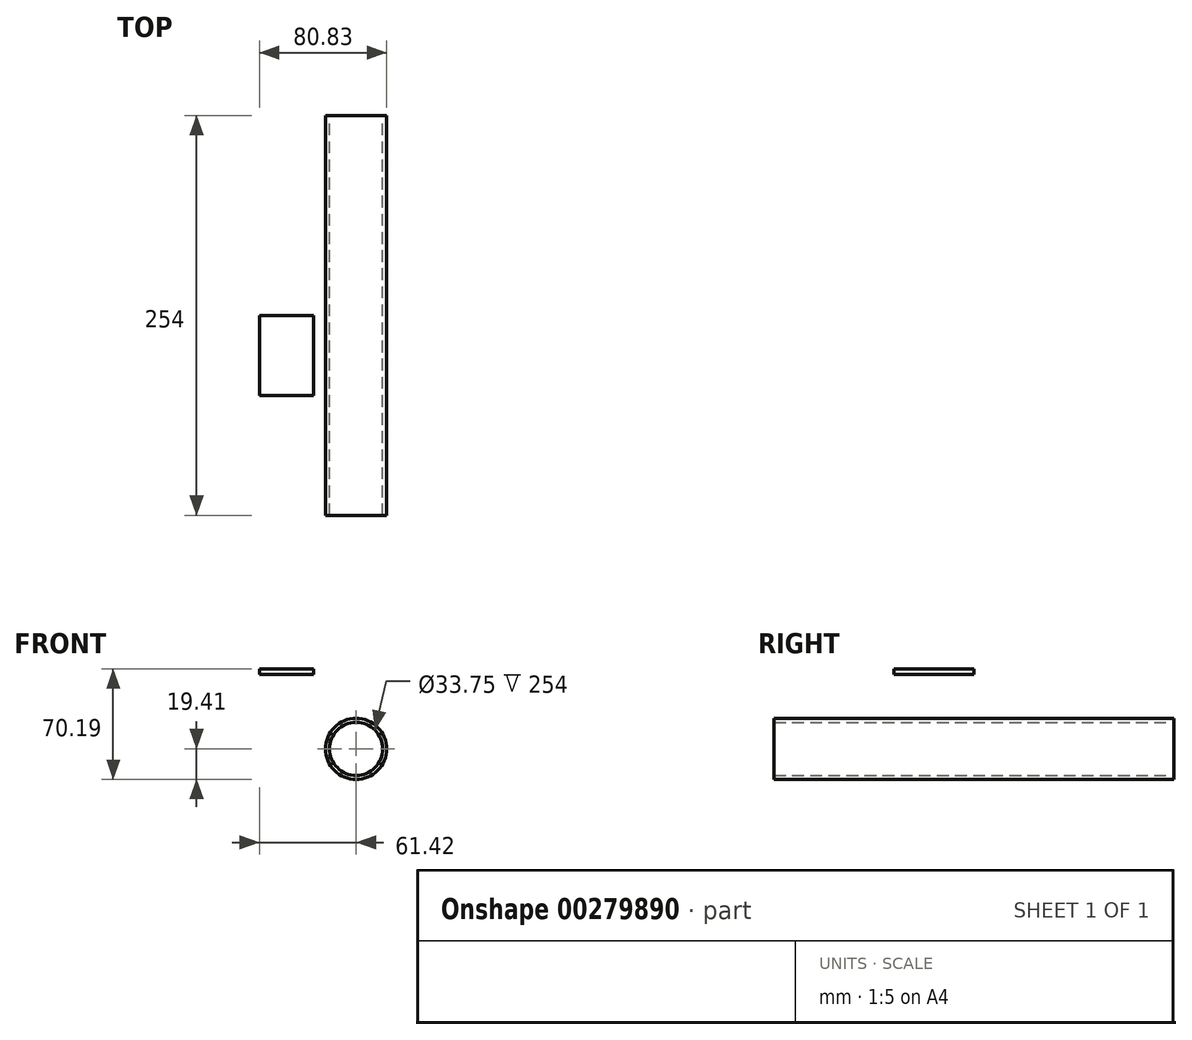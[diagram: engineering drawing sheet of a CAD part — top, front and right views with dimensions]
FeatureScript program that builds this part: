
annotation { "Feature Type Name" : "Feature", "Feature Type Description" : "" }
export const myFeature = defineFeature(function(context is Context, id is Id, definition is map)
    precondition{}
    {
        {
            var Q0;
            Q0=qCreatedBy(makeId("Front.planeOp"),FACE);
            var sketch = newSketch(context, id + "F0", { "sketchPlane" : qUnion([Q0])});
            skCircle(sketch, "E0", {"center": v(0, 0) * mm, "radius": 19.4 * mm});
            skCircle(sketch, "E1", {"center": v(0, 0) * mm, "radius": 16.88 * mm});
            skLineSegment(sketch, "E2.bottom", {"start": v(-61.42, 50.78) * mm, "end": v(-27, 50.78) * mm});
            skLineSegment(sketch, "E2.top", {"start": v(-61.42, 47.27) * mm, "end": v(-27, 47.27) * mm});
            skLineSegment(sketch, "E2.left", {"start": v(-61.42, 50.78) * mm, "end": v(-61.42, 47.27) * mm});
            skLineSegment(sketch, "E2.right", {"start": v(-27, 50.78) * mm, "end": v(-27, 47.27) * mm});
            skPoint(sketch, "E3", {"position": v(0, 19.4) * mm});
            skPoint(sketch, "E4.1.0", {"position": v(16.8, -9.7) * mm});
            skPoint(sketch, "E4.2.0", {"position": v(-16.8, -9.7) * mm});
            skLineSegment(sketch, "E4.anchor1", {"start": v(0, 0) * mm, "end": v(0, 19.4) * mm, "construction": true});
            skLineSegment(sketch, "E4.anchor2", {"start": v(0, 0) * mm, "end": v(-16.8, -9.7) * mm, "construction": true});
            skSolve(sketch);
        }
        {
            var Q0;
            Q0=makeQuery(id+"F0.imprint","IMPRINT",FACE,{"disambiguationData":[TD([[makeQuery(id+"F0.imprint","IMPRINT",EDGE,{"derivedFrom":sQuery(id+"F0.wireOp",EDGE,"E1")}),-1.0]])]});
            var Q1;
            Q1=sQuery(id+"F0.wireOp",EDGE,"E0");
            var Q2;
            Q2=sQuery(id+"F0.wireOp",EDGE,"E1");
            extrude(context, id + "F1", {"entities" : qUnion([Q0]), "surfaceEntities" : qUnion([Q1, Q2]), "endBound" : BoundingType.SYMMETRIC, "depth" : 254 * mm});
        }
        {
            var Q0;
            Q0=makeQuery(id+"F0.imprint","IMPRINT",FACE,{"disambiguationData":[TD([[makeQuery(id+"F0.imprint","IMPRINT",EDGE,{"derivedFrom":sQuery(id+"F0.wireOp",EDGE,"E2.bottom")}),-1.0]])]});
            extrude(context, id + "F2", {"entities" : qUnion([Q0]), "depth" : 50.8 * mm});
        }
    });
